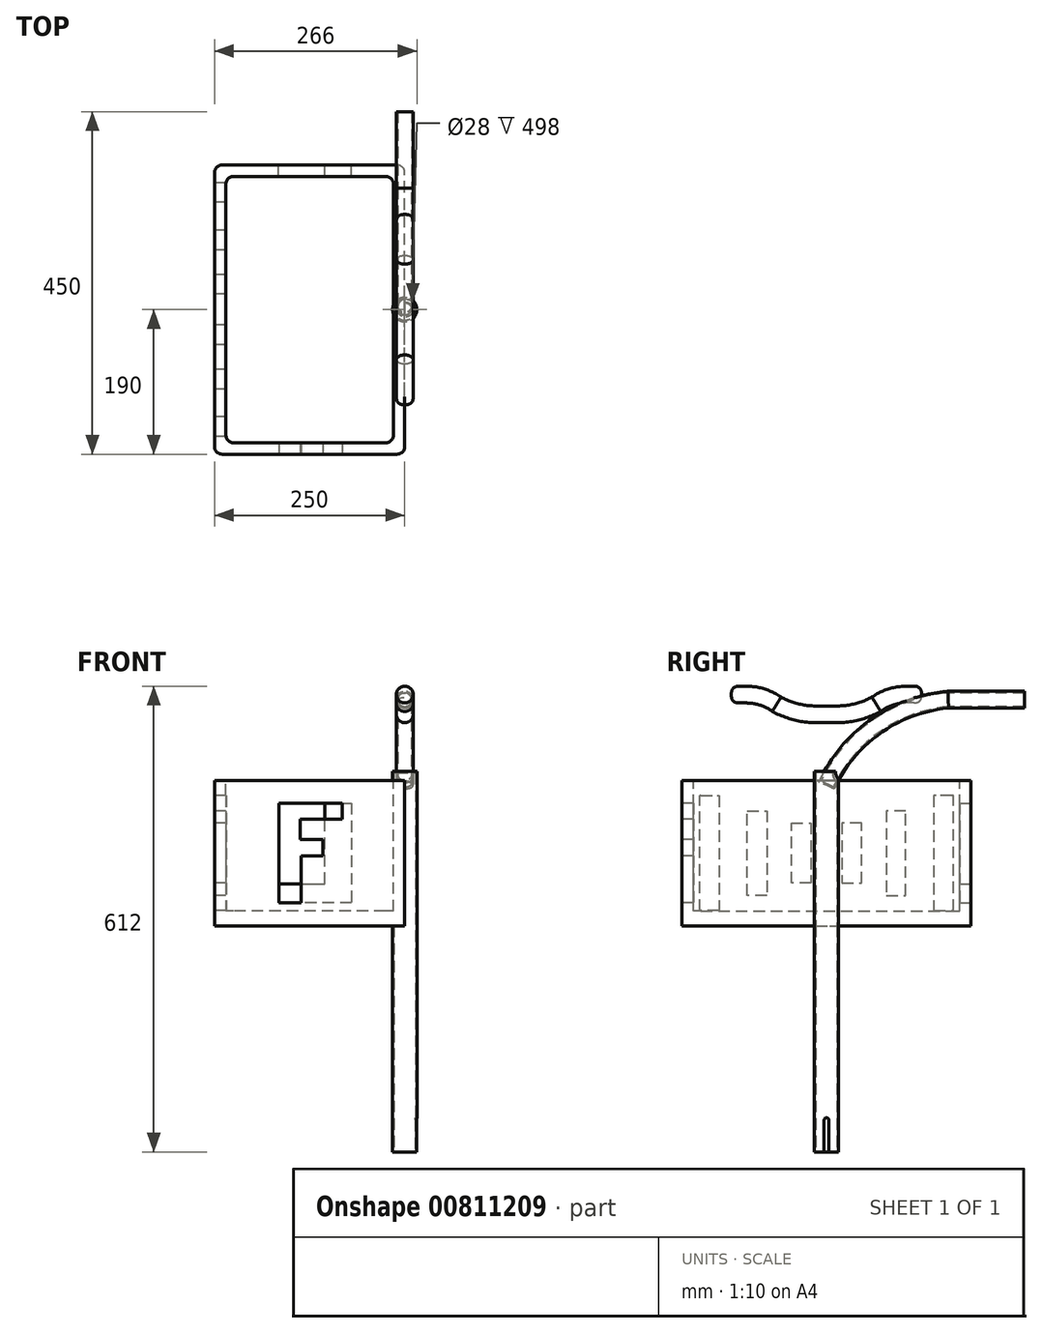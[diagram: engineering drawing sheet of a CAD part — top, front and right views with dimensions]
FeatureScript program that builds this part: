
annotation { "Feature Type Name" : "Feature", "Feature Type Description" : "" }
export const myFeature = defineFeature(function(context is Context, id is Id, definition is map)
    precondition{}
    {
        {
            var Q0;
            Q0=qCreatedBy(makeId("Top.planeOp"),FACE);
            var sketch = newSketch(context, id + "F0", { "sketchPlane" : qUnion([Q0])});
            skCircle(sketch, "E0", {"center": v(0, 0) * mm, "radius": 16 * mm});
            skSolve(sketch);
        }
        {
            var Q0;
            Q0 = qSketchRegion(id + "F0", true);
            extrude(context, id + "F1", {"entities" : qUnion([Q0]), "depth" : 500 * mm, "offsetDistance" : 25 * mm});
        }
        {
            var Q0;
            Q0=makeQuery(id+"F1.opExtrude","CAP_FACE",FACE,{"disambiguationData":[OSD([sQuery(id+"F0.wireOp",EDGE,"E0")])],"isStart":true});
            shell(context, id + "F2", {"entities" : qUnion([Q0]), "thickness" : 2 * mm});
        }
        {
            var Q0;
            Q0=qCreatedBy(makeId("Right.planeOp"),FACE);
            var sketch = newSketch(context, id + "F3", { "sketchPlane" : qUnion([Q0])});
            skLineSegment(sketch, "E1.bottom", {"start": v(3, 0) * mm, "end": v(-3, 0) * mm});
            skLineSegment(sketch, "E1.top", {"start": v(0, 45) * mm, "end": v(0, 45) * mm});
            skLineSegment(sketch, "E1.left", {"start": v(3, 0) * mm, "end": v(3, 42) * mm});
            skLineSegment(sketch, "E1.right", {"start": v(-3, 0) * mm, "end": v(-3, 42) * mm});
            skPoint(sketch, "E2.visualSharp", {"position": v(-3, 45) * mm});
            skArc(sketch, "E2.filletArc", {"start": v(0, 45) * mm, "mid": v(-2.12, 44.12) * mm, "end": v(-3, 42) * mm});
            skPoint(sketch, "E3.visualSharp", {"position": v(3, 45) * mm});
            skArc(sketch, "E3.filletArc", {"start": v(3, 42) * mm, "mid": v(2.12, 44.12) * mm, "end": v(0, 45) * mm});
            skSolve(sketch);
        }
        {
            var Q0;
            Q0 = qSketchRegion(id + "F3", true);
            extrude(context, id + "F4", {"entities" : qUnion([Q0]), "operationType" : NewBodyOperationType.REMOVE, "endBound" : BoundingType.THROUGH_ALL, "depth" : 25 * mm, "offsetDistance" : 25 * mm});
        }
        {
            var Q0;
            Q0=qCreatedBy(makeId("Right.planeOp"),FACE);
            var sketch = newSketch(context, id + "F5", { "sketchPlane" : qUnion([Q0])});
            skArc(sketch, "E4", {"start": v(160, 594.25) * mm, "mid": v(64.87, 559.51) * mm, "end": v(0, 481.75) * mm});
            skLineSegment(sketch, "E5", {"start": v(160, 594.25) * mm, "end": v(260, 594.25) * mm});
            skSolve(sketch);
        }
        {
            var Q0;
            Q0=sQuery(id+"F5.wireOp",VERTEX,"E5.end");
            var Q1;
            Q1=qCreatedBy(makeId("Front.planeOp"),FACE);
            cPlane(context, id + "F6", {"entities" : qUnion([Q0, Q1]), "cplaneType" : CPlaneType.PLANE_POINT, "offset" : 25 * mm, "width" : 150 * mm, "height" : 150 * mm});
        }
        {
            var Q0;
            Q0=qCreatedBy(id+"F6.planeOp",FACE);
            var sketch = newSketch(context, id + "F7", { "sketchPlane" : qUnion([Q0])});
            skCircle(sketch, "E6", {"center": v(0, 594.25) * mm, "radius": 11 * mm});
            skSolve(sketch);
        }
        {
            var Q0;
            Q0 = qSketchRegion(id + "F7", true);
            var Q1;
            Q1 = qConstructionFilter(qBodyType(qCreatedBy(id + "F5" ,EDGE), BodyType.WIRE), ConstructionObject.NO);
            sweep(context, id + "F8", {"operationType" : NewBodyOperationType.ADD, "profiles" : qUnion([Q0]), "path" : qUnion([Q1])});
        }
        {
            var Q0;
            Q0=makeQuery(id+"F8.opSweep","CAP_FACE",FACE,{"disambiguationData":[OSD([sQuery(id+"F5.wireOp",VERTEX,"E5.end"),sQuery(id+"F7.wireOp",EDGE,"E6")])],"isStart":true});
            shell(context, id + "F9", {"entities" : qUnion([Q0]), "thickness" : 2 * mm});
        }
        {
            var Q0;
            Q0=qCreatedBy(makeId("Right.planeOp"),FACE);
            var sketch = newSketch(context, id + "F10", { "sketchPlane" : qUnion([Q0])});
            skLineSegment(sketch, "E7", {"start": v(0, 487.04) * mm, "end": v(0, 575) * mm, "construction": true});
            skLineSegment(sketch, "E8", {"start": v(-125, 601) * mm, "end": v(-105, 601) * mm});
            skArc(sketch, "E9", {"start": v(-65.42, 588.23) * mm, "mid": v(-84.2, 597.73) * mm, "end": v(-105, 601) * mm});
            skArc(sketch, "E10", {"start": v(-65.42, 588.23) * mm, "mid": v(-39.78, 578.35) * mm, "end": v(-12.5, 575) * mm});
            skLineSegment(sketch, "E11", {"start": v(-12.5, 575) * mm, "end": v(0, 575) * mm});
            skArc(sketch, "E12.MirrorCS", {"start": v(65.42, 588.23) * mm, "mid": v(39.78, 578.35) * mm, "end": v(12.5, 575) * mm});
            skArc(sketch, "E13.MirrorCS", {"start": v(65.42, 588.23) * mm, "mid": v(84.2, 597.73) * mm, "end": v(105, 601) * mm});
            skLineSegment(sketch, "E14.MirrorCS", {"start": v(125, 601) * mm, "end": v(105, 601) * mm});
            skLineSegment(sketch, "E15", {"start": v(0, 575) * mm, "end": v(12.5, 575) * mm});
            skSolve(sketch);
        }
        {
            var Q0;
            Q0=sQuery(id+"F10.wireOp",VERTEX,"E14.MirrorCS.start");
            var Q1;
            Q1=qCreatedBy(id+"F6.planeOp",FACE);
            cPlane(context, id + "F11", {"entities" : qUnion([Q0, Q1]), "cplaneType" : CPlaneType.PLANE_POINT, "offset" : 25 * mm, "width" : 150 * mm, "height" : 150 * mm});
        }
        {
            var Q0;
            Q0=qCreatedBy(id+"F11.planeOp",FACE);
            var sketch = newSketch(context, id + "F12", { "sketchPlane" : qUnion([Q0])});
            skCircle(sketch, "E16", {"center": v(0, 601) * mm, "radius": 11 * mm});
            skSolve(sketch);
        }
        {
            var Q0;
            Q0 = qSketchRegion(id + "F12", true);
            var Q1;
            Q1 = qConstructionFilter(qBodyType(qCreatedBy(id + "F10" ,EDGE), BodyType.WIRE), ConstructionObject.NO);
            sweep(context, id + "F13", {"profiles" : qUnion([Q0]), "path" : qUnion([Q1])});
        }
        {
            var Q0;
            Q0=makeQuery(id+"F13.opSweep","CAP_EDGE",EDGE,{"disambiguationData":[OSD([sQuery(id+"F10.wireOp",VERTEX,"E8.start"),sQuery(id+"F12.wireOp",EDGE,"E16")])],"isStart":false});
            var Q1;
            Q1=makeQuery(id+"F13.opSweep","CAP_EDGE",EDGE,{"disambiguationData":[OSD([sQuery(id+"F10.wireOp",VERTEX,"E14.MirrorCS.start"),sQuery(id+"F12.wireOp",EDGE,"E16")])],"isStart":true});
            fillet(context, id + "F14", {"entities" : qUnion([Q0, Q1]), "radius" : 10 * mm, "tangentPropagation" : true, "rho" : 0.5, "crossSection" : FilletCrossSection.CONIC, "allowEdgeOverflow" : false});
        }
        {
            var Q0;
            Q0=qCreatedBy(makeId("Right.planeOp"),FACE);
            var sketch = newSketch(context, id + "F15", { "sketchPlane" : qUnion([Q0])});
            skLineSegment(sketch, "E17", {"start": v(-190, 488.35) * mm, "end": v(-190, 297.16) * mm});
            skLineSegment(sketch, "E18", {"start": v(-190, 297.16) * mm, "end": v(190, 297.16) * mm});
            skLineSegment(sketch, "E19", {"start": v(190, 297.16) * mm, "end": v(190, 488.35) * mm});
            skLineSegment(sketch, "E20", {"start": v(-190, 488.35) * mm, "end": v(190, 488.35) * mm});
            skSolve(sketch);
        }
        {
            var Q0;
            Q0 = qSketchRegion(id + "F15", true);
            extrude(context, id + "F16", {"entities" : qUnion([Q0]), "operationType" : NewBodyOperationType.ADD, "oppositeDirection" : true, "depth" : 250 * mm, "offsetDistance" : 25 * mm});
        }
        {
            var Q0;
            {var subQ0=sQuery(id+"F15.wireOp",EDGE,"E20");Q0=makeQuery(id+"F16.boolean.opBoolean","SPLIT",FACE,{"disambiguationData":[TD([makeQuery(id+"F1.opExtrude","SWEPT_FACE",FACE,{"disambiguationData":[OSD([sQuery(id+"F0.wireOp",EDGE,"E0")])]})])],"derivedFrom":makeQuery(id+"F16.opExtrude","SWEPT_FACE",FACE,{"disambiguationData":[OSD([subQ0])]})});}
            var sketch = newSketch(context, id + "F17", { "sketchPlane" : qUnion([Q0])});
            skLineSegment(sketch, "E21", {"start": v(-235, 175) * mm, "end": v(-15, 175) * mm});
            skLineSegment(sketch, "E22", {"start": v(-235, -175) * mm, "end": v(-235, 175) * mm});
            skLineSegment(sketch, "E23", {"start": v(-15, -175) * mm, "end": v(-235, -175) * mm});
            skLineSegment(sketch, "E24", {"start": v(-15, 175) * mm, "end": v(-15, -175) * mm});
            skSolve(sketch);
        }
        {
            var Q0;
            Q0 = qSketchRegion(id + "F17", true);
            var Q1;
            {var subQ2=sQuery(id+"F15.wireOp",EDGE,"E18");Q1=makeQuery(id+"F16.boolean.opBoolean","SPLIT",FACE,{"disambiguationData":[TD([makeQuery(id+"F1.opExtrude","SWEPT_FACE",FACE,{"disambiguationData":[OSD([sQuery(id+"F0.wireOp",EDGE,"E0")])]})])],"derivedFrom":makeQuery(id+"F16.opExtrude","SWEPT_FACE",FACE,{"disambiguationData":[OSD([subQ2])]})});}
            extrude(context, id + "F18", {"entities" : qUnion([Q0]), "operationType" : NewBodyOperationType.REMOVE, "oppositeDirection" : true, "depth" : 172 * mm, "endBoundEntityFace" : qUnion([Q1]), "offsetDistance" : 25 * mm});
        }
        {
            var Q0;
            Q0=makeQuery(id+"F16.opExtrude","CAP_FACE",FACE,{"disambiguationData":[OSD([sQuery(id+"F15.wireOp",EDGE,"E17"),sQuery(id+"F15.wireOp",EDGE,"E18"),sQuery(id+"F15.wireOp",EDGE,"E19"),sQuery(id+"F15.wireOp",EDGE,"E20")])],"isStart":false});
            var sketch = newSketch(context, id + "F19", { "sketchPlane" : qUnion([Q0])});
            skLineSegment(sketch, "E25", {"start": v(-166.78, 468.35) * mm, "end": v(-141.05, 468.35) * mm});
            skLineSegment(sketch, "E26", {"start": v(-141.05, 468.35) * mm, "end": v(-141.05, 317.16) * mm});
            skLineSegment(sketch, "E27", {"start": v(-141.05, 317.16) * mm, "end": v(-166.78, 317.16) * mm});
            skLineSegment(sketch, "E28", {"start": v(-166.78, 317.16) * mm, "end": v(-166.78, 468.35) * mm});
            skLineSegment(sketch, "E29", {"start": v(-104.28, 448.35) * mm, "end": v(-78.55, 448.35) * mm});
            skLineSegment(sketch, "E30", {"start": v(-78.55, 448.35) * mm, "end": v(-78.55, 337.16) * mm});
            skLineSegment(sketch, "E31", {"start": v(-78.55, 337.16) * mm, "end": v(-104.28, 337.16) * mm});
            skLineSegment(sketch, "E32", {"start": v(-104.28, 337.16) * mm, "end": v(-104.28, 448.35) * mm});
            skLineSegment(sketch, "E33", {"start": v(-46.07, 432.35) * mm, "end": v(-20.34, 432.35) * mm});
            skLineSegment(sketch, "E34", {"start": v(-20.34, 432.35) * mm, "end": v(-20.34, 353.16) * mm});
            skLineSegment(sketch, "E35", {"start": v(-20.34, 353.16) * mm, "end": v(-46.07, 353.16) * mm});
            skLineSegment(sketch, "E36", {"start": v(-46.07, 353.16) * mm, "end": v(-46.07, 432.35) * mm});
            skLineSegment(sketch, "E37.MirrorCS", {"start": v(20.34, 432.35) * mm, "end": v(20.34, 353.16) * mm});
            skLineSegment(sketch, "E38.MirrorCS", {"start": v(20.34, 353.16) * mm, "end": v(46.07, 353.16) * mm});
            skLineSegment(sketch, "E39.MirrorCS", {"start": v(46.07, 432.35) * mm, "end": v(20.34, 432.35) * mm});
            skLineSegment(sketch, "E40.MirrorCS", {"start": v(46.07, 353.16) * mm, "end": v(46.07, 432.35) * mm});
            skLineSegment(sketch, "E41.MirrorCS", {"start": v(78.55, 448.35) * mm, "end": v(78.55, 337.16) * mm});
            skLineSegment(sketch, "E42.MirrorCS", {"start": v(104.28, 448.35) * mm, "end": v(78.55, 448.35) * mm});
            skLineSegment(sketch, "E43.MirrorCS", {"start": v(104.28, 337.16) * mm, "end": v(104.28, 448.35) * mm});
            skLineSegment(sketch, "E44.MirrorCS", {"start": v(78.55, 337.16) * mm, "end": v(104.28, 337.16) * mm});
            skLineSegment(sketch, "E45.MirrorCS", {"start": v(141.05, 317.16) * mm, "end": v(166.78, 317.16) * mm});
            skLineSegment(sketch, "E46.MirrorCS", {"start": v(141.05, 468.35) * mm, "end": v(141.05, 317.16) * mm});
            skLineSegment(sketch, "E47.MirrorCS", {"start": v(166.78, 317.16) * mm, "end": v(166.78, 468.35) * mm});
            skLineSegment(sketch, "E48.MirrorCS", {"start": v(166.78, 468.35) * mm, "end": v(141.05, 468.35) * mm});
            skSolve(sketch);
        }
        {
            var Q0;
            Q0 = qSketchRegion(id + "F19", true);
            var Q1;
            Q1=makeQuery(id+"F18.boolean.opBoolean","COPY",FACE,{"derivedFrom":makeQuery(id+"F18.opExtrude","SWEPT_FACE",FACE,{"disambiguationData":[OSD([sQuery(id+"F17.wireOp",EDGE,"E22")])]})});
            extrude(context, id + "F20", {"entities" : qUnion([Q0]), "operationType" : NewBodyOperationType.REMOVE, "endBound" : BoundingType.UP_TO_SURFACE, "oppositeDirection" : true, "depth" : 25 * mm, "endBoundEntityFace" : qUnion([Q1]), "offsetDistance" : 25 * mm});
        }
        {
            var Q0;
            Q0=makeQuery(id+"F16.opExtrude","SWEPT_FACE",FACE,{"disambiguationData":[OSD([sQuery(id+"F15.wireOp",EDGE,"E19")])]});
            var sketch = newSketch(context, id + "F21", { "sketchPlane" : qUnion([Q0])});
            skLineSegment(sketch, "E49", {"start": v(70, 458.35) * mm, "end": v(70, 327.16) * mm});
            skLineSegment(sketch, "E50", {"start": v(70, 327.16) * mm, "end": v(166, 327.16) * mm});
            skLineSegment(sketch, "E51", {"start": v(166, 327.16) * mm, "end": v(166, 352.16) * mm});
            skLineSegment(sketch, "E52", {"start": v(166, 352.16) * mm, "end": v(105, 352.16) * mm});
            skLineSegment(sketch, "E53", {"start": v(105, 352.16) * mm, "end": v(105, 458.35) * mm});
            skLineSegment(sketch, "E54", {"start": v(105, 458.35) * mm, "end": v(70, 458.35) * mm});
            skSolve(sketch);
        }
        {
            var Q0;
            Q0 = qSketchRegion(id + "F21", true);
            var Q1;
            Q1=makeQuery(id+"F18.boolean.opBoolean","COPY",FACE,{"derivedFrom":makeQuery(id+"F18.opExtrude","SWEPT_FACE",FACE,{"disambiguationData":[OSD([sQuery(id+"F17.wireOp",EDGE,"E21")])]})});
            extrude(context, id + "F22", {"entities" : qUnion([Q0]), "operationType" : NewBodyOperationType.REMOVE, "endBound" : BoundingType.UP_TO_SURFACE, "oppositeDirection" : true, "depth" : 25 * mm, "endBoundEntityFace" : qUnion([Q1]), "offsetDistance" : 25 * mm});
        }
        {
            var Q0;
            Q0=makeQuery(id+"F16.opExtrude","SWEPT_FACE",FACE,{"disambiguationData":[OSD([sQuery(id+"F15.wireOp",EDGE,"E17")])]});
            var sketch = newSketch(context, id + "F23", { "sketchPlane" : qUnion([Q0])});
            skLineSegment(sketch, "E55", {"start": v(-165.26, 327.16) * mm, "end": v(-165.26, 458.35) * mm});
            skLineSegment(sketch, "E56", {"start": v(-165.26, 458.35) * mm, "end": v(-82.51, 458.35) * mm});
            skLineSegment(sketch, "E57", {"start": v(-82.51, 458.35) * mm, "end": v(-82.51, 437) * mm});
            skLineSegment(sketch, "E58", {"start": v(-82.51, 437) * mm, "end": v(-137.23, 437) * mm});
            skLineSegment(sketch, "E59", {"start": v(-137.23, 437) * mm, "end": v(-137.23, 410.3) * mm});
            skLineSegment(sketch, "E60", {"start": v(-137.23, 410.3) * mm, "end": v(-107.87, 410.3) * mm});
            skLineSegment(sketch, "E61", {"start": v(-107.87, 410.3) * mm, "end": v(-107.87, 388.95) * mm});
            skLineSegment(sketch, "E62", {"start": v(-107.87, 388.95) * mm, "end": v(-135.9, 388.95) * mm});
            skLineSegment(sketch, "E63", {"start": v(-135.9, 388.95) * mm, "end": v(-135.9, 327.16) * mm});
            skLineSegment(sketch, "E64", {"start": v(-135.9, 327.16) * mm, "end": v(-165.26, 327.16) * mm});
            skSolve(sketch);
        }
        {
            var Q0;
            Q0 = qSketchRegion(id + "F23", true);
            var Q1;
            Q1=makeQuery(id+"F18.boolean.opBoolean","COPY",FACE,{"derivedFrom":makeQuery(id+"F18.opExtrude","SWEPT_FACE",FACE,{"disambiguationData":[OSD([sQuery(id+"F17.wireOp",EDGE,"E23")])]})});
            extrude(context, id + "F24", {"entities" : qUnion([Q0]), "operationType" : NewBodyOperationType.REMOVE, "endBound" : BoundingType.UP_TO_SURFACE, "oppositeDirection" : true, "depth" : 25 * mm, "endBoundEntityFace" : qUnion([Q1]), "offsetDistance" : 25 * mm});
        }
        {
            var Q0;
            Q0=makeQuery(id+"F16.opExtrude","CAP_EDGE",EDGE,{"disambiguationData":[OSD([sQuery(id+"F15.wireOp",EDGE,"E19")])],"isStart":false});
            var Q1;
            Q1=makeQuery(id+"F16.opExtrude","CAP_EDGE",EDGE,{"disambiguationData":[OSD([sQuery(id+"F15.wireOp",EDGE,"E19")])],"isStart":true});
            var Q2;
            Q2=makeQuery(id+"F16.opExtrude","CAP_EDGE",EDGE,{"disambiguationData":[OSD([sQuery(id+"F15.wireOp",EDGE,"E17")])],"isStart":false});
            var Q3;
            Q3=makeQuery(id+"F16.opExtrude","CAP_EDGE",EDGE,{"disambiguationData":[OSD([sQuery(id+"F15.wireOp",EDGE,"E17")])],"isStart":true});
            var Q4;
            Q4=makeQuery(id+"F18.boolean.opBoolean","COPY",EDGE,{"derivedFrom":makeQuery(id+"F18.opExtrude","SWEPT_EDGE",EDGE,{"disambiguationData":[OSD([sQuery(id+"F17.wireOp",EDGE,"E21"),sQuery(id+"F17.wireOp",EDGE,"E22")])]})});
            var Q5;
            Q5=makeQuery(id+"F18.boolean.opBoolean","COPY",EDGE,{"derivedFrom":makeQuery(id+"F18.opExtrude","SWEPT_EDGE",EDGE,{"disambiguationData":[OSD([sQuery(id+"F17.wireOp",EDGE,"E22"),sQuery(id+"F17.wireOp",EDGE,"E23")])]})});
            var Q6;
            Q6=makeQuery(id+"F18.boolean.opBoolean","COPY",EDGE,{"derivedFrom":makeQuery(id+"F18.opExtrude","SWEPT_EDGE",EDGE,{"disambiguationData":[OSD([sQuery(id+"F17.wireOp",EDGE,"E23"),sQuery(id+"F17.wireOp",EDGE,"E24")])]})});
            var Q7;
            Q7=makeQuery(id+"F18.boolean.opBoolean","COPY",EDGE,{"derivedFrom":makeQuery(id+"F18.opExtrude","SWEPT_EDGE",EDGE,{"disambiguationData":[OSD([sQuery(id+"F17.wireOp",EDGE,"E21"),sQuery(id+"F17.wireOp",EDGE,"E24")])]})});
            fillet(context, id + "F25", {"entities" : qUnion([Q0, Q1, Q2, Q3, Q4, Q5, Q6, Q7]), "radius" : 10 * mm, "tangentPropagation" : true, "allowEdgeOverflow" : false});
        }
    });
